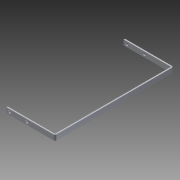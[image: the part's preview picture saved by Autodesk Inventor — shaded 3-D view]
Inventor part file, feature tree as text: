
AUTODESK INVENTOR PART (.ipt)
format: ipt  version: 2013 (Build 170138000, 138)  size: 206,848 bytes
history: native  units: in
note: dims shown in document units (in); Inventor stores cm internally (conversion verified against a paired STEP export)
features: sheet_metal_op x7, sketch x7, other x6, extrude x2, reference x2
ambient origin geometry x8: Origin, YZ Plane, XZ Plane, XY Plane, X Axis, Y Axis, Z Axis, Center Point
feature tree (24):
  sheet_metal_op  "Face2"
  sheet_metal_op  "Flange4"
  sheet_metal_op  "Flange5"
  extrude  "Extrusion3"  Depth=0.5in
  extrude  "Extrusion4"  Depth=0.125in
  sketch  "Sketch1"  dims[d1=4.494in d2=0.5in]
  other  "Plate5"
  sketch  "Sketch6"  dims[d42=0.125in]
  other  "Plate6"
  sheet_metal_op  "Bend4"
  sheet_metal_op  "Corner4"
  sketch  "Sketch7"  dims[d43=0.125in]
  other  "Plate7"
  sheet_metal_op  "Bend5"
  sheet_metal_op  "Corner5"
  sketch  "Sketch12"  dims[d44=0.0625in]
  sketch  "Sketch13"  dims[d45=0.25in]
  reference  "Reference3"
  reference  "Reference4"
  sketch  "Sketch14"  dims[d46=0.125in d47=11.218in d48=90.0deg d49=0.05in d50=0.5in d51=0.125in d52=0.125in d53=0.125in d54=0.0625in d55=0.25in d56=0.125in d57=4.669in d58=90.0deg d59=0.05in d60=0.5in d61=0.125in d62=0.125in d66=0.26in d67=0.295in d70=1.9482in d71=999.0in d72=0.0in d73=0.125in d74=0.0in d75=20.0in d76=0.0in d0=4.576in d3=0.0625in d4=0.0625in d6=0.0312in d7=4.576in d9=0.0312in d10=0.0625in d11=0.125in d12=0.0in d13=0.0312in d14=0.125in d15=0.0in]
  other  "Cut1"
  other  "Definition1"
  sketch  "Sketch2"  dims[d5=0.295in d8=0.125in]
  other  "Cut2"
